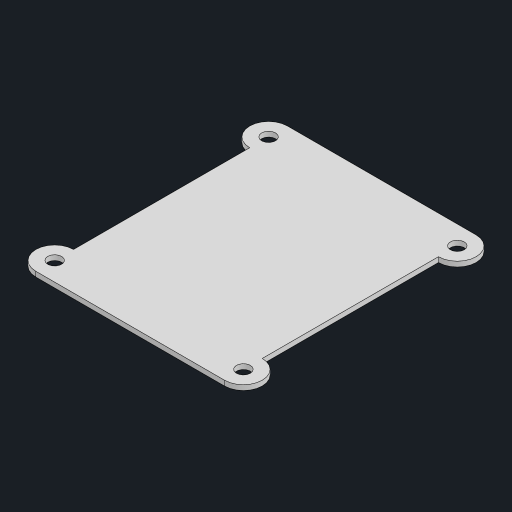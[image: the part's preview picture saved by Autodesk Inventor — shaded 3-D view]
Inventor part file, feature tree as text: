
AUTODESK INVENTOR PART (.ipt)
format: ipt  version: 2023 (Build 270158000, 158)  size: 116,736 bytes
history: native  units: mm
features: mirror x2, other x1, extrude x1, sketch x1
ambient origin geometry x8: Origin, YZ Plane, XZ Plane, XY Plane, X Axis, Y Axis, Z Axis, Center Point
bodies: Body1 (feature_tree)
feature tree (5):
  other  "ソリッド1"
  extrude  "押し出し1"  Depth=30.0mm
  mirror  "ミラー1"
  mirror  "ミラー2"
  sketch  "スケッチ1"
